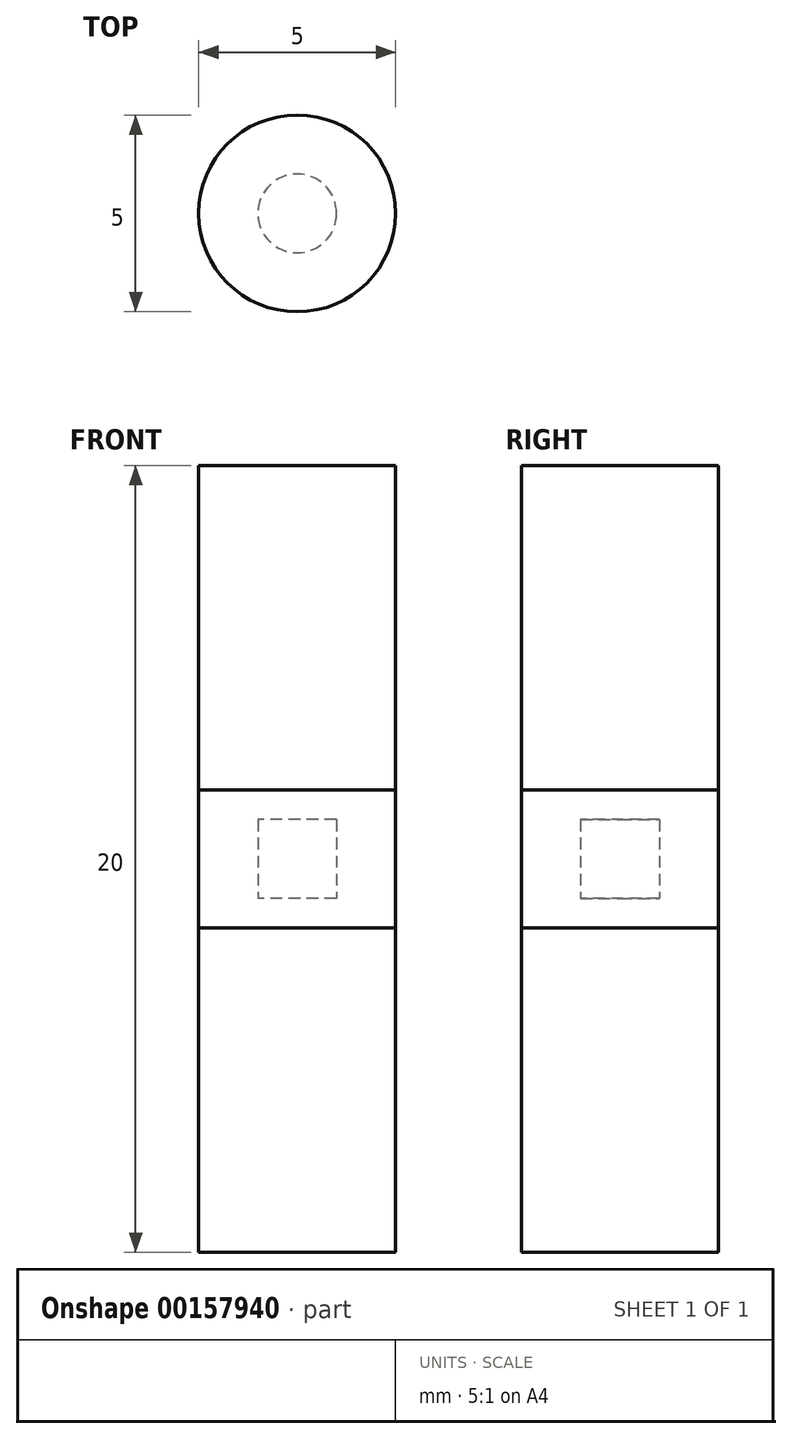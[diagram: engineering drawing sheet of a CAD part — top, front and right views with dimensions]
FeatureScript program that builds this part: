
annotation { "Feature Type Name" : "Feature", "Feature Type Description" : "" }
export const myFeature = defineFeature(function(context is Context, id is Id, definition is map)
    precondition{}
    {
        {
            assignVariable(context, id + "F0", {"name" : "h", "anyValue" : 2});
        }
        {
            var Q0;
            Q0=qCreatedBy(makeId("Top.planeOp"),FACE);
            var sketch = newSketch(context, id + "F1", { "sketchPlane" : qUnion([Q0])});
            skCircle(sketch, "E0", {"center": v(0, 0) * mm, "radius": 1 * mm});
            skSolve(sketch);
        }
        {
            var Q0;
            Q0=makeQuery(id+"F1.imprint","IMPRINT",FACE,{"disambiguationData":[TD([[makeQuery(id+"F1.imprint","IMPRINT",EDGE,{"derivedFrom":sQuery(id+"F1.wireOp",EDGE,"E0")}),1.0]])]});
            extrude(context, id + "F2", {"entities" : qUnion([Q0]), "endBound" : BoundingType.SYMMETRIC, "depth" : (getVariable(context, 'h')) * mm});
        }
        {
            assignVariable(context, id + "F3", {"name" : "h2", "anyValue" : 3.5});
        }
        {
            var Q0;
            Q0=qCreatedBy(makeId("Top.planeOp"),FACE);
            var sketch = newSketch(context, id + "F4", { "sketchPlane" : qUnion([Q0])});
            skCircle(sketch, "E1", {"center": v(0, 0) * mm, "radius": 2.5 * mm});
            skSolve(sketch);
        }
        {
            var Q0;
            Q0=makeQuery(id+"F4.imprint","IMPRINT",FACE,{"disambiguationData":[TD([[makeQuery(id+"F4.imprint","IMPRINT",EDGE,{"derivedFrom":sQuery(id+"F4.wireOp",EDGE,"E1")}),1.0]])]});
            extrude(context, id + "F5", {"entities" : qUnion([Q0]), "endBound" : BoundingType.SYMMETRIC, "depth" : (getVariable(context, 'h2')) * mm});
        }
        {
            var Q0;
            Q0=makeQuery(id+"F4.imprint","IMPRINT",FACE,{"disambiguationData":[TD([[makeQuery(id+"F4.imprint","IMPRINT",EDGE,{"derivedFrom":sQuery(id+"F4.wireOp",EDGE,"E1")}),1.0]])]});
            extrude(context, id + "F6", {"entities" : qUnion([Q0]), "endBound" : BoundingType.SYMMETRIC, "depth" : 20 * mm});
        }
    });
